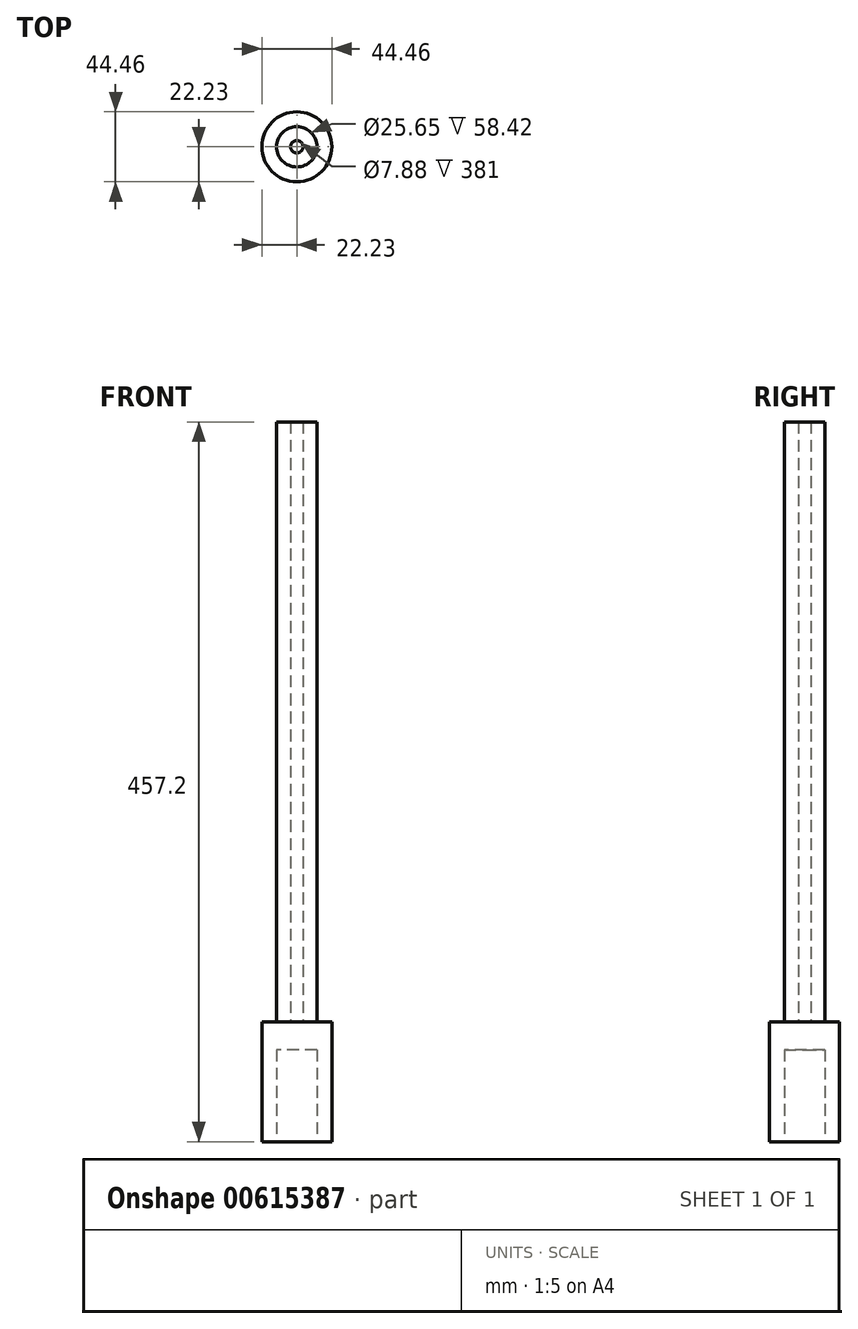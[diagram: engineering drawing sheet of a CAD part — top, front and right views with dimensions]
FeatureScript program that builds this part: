
annotation { "Feature Type Name" : "Feature", "Feature Type Description" : "" }
export const myFeature = defineFeature(function(context is Context, id is Id, definition is map)
    precondition{}
    {
        {
            var Q0;
            Q0=qCreatedBy(makeId("Top.planeOp"),FACE);
            var sketch = newSketch(context, id + "F0", { "sketchPlane" : qUnion([Q0])});
            skCircle(sketch, "E0", {"center": v(0, 0) * mm, "radius": 22.23 * mm});
            skCircle(sketch, "E1", {"center": v(0, 0) * mm, "radius": 12.83 * mm});
            skCircle(sketch, "E2", {"center": v(0, 0) * mm, "radius": 3.94 * mm});
            skSolve(sketch);
        }
        {
            var Q0;
            Q0=qSketchRegion(id+"F0",true);
            var Q1;
            Q1=makeQuery(id+"F0.imprint","IMPRINT",FACE,{"disambiguationData":[TD([[makeQuery(id+"F0.imprint","IMPRINT",EDGE,{"derivedFrom":sQuery(id+"F0.wireOp",EDGE,"E1")}),1.0]])]});
            var Q2;
            Q2=makeQuery(id+"F0.imprint","IMPRINT",FACE,{"disambiguationData":[TD([[makeQuery(id+"F0.imprint","IMPRINT",EDGE,{"derivedFrom":sQuery(id+"F0.wireOp",EDGE,"E2")}),1.0]])]});
            extrude(context, id + "F1", {"entities" : qUnion([Q0, Q1, Q2]), "depth" : 76.2 * mm, "offsetDistance" : 25.4 * mm});
        }
        {
            var Q0;
            Q0=makeQuery(id+"F0.imprint","IMPRINT",FACE,{"disambiguationData":[TD([[makeQuery(id+"F0.imprint","IMPRINT",EDGE,{"derivedFrom":sQuery(id+"F0.wireOp",EDGE,"E1")}),1.0]])]});
            var Q1;
            Q1=makeQuery(id+"F0.imprint","IMPRINT",FACE,{"disambiguationData":[TD([[makeQuery(id+"F0.imprint","IMPRINT",EDGE,{"derivedFrom":sQuery(id+"F0.wireOp",EDGE,"E2")}),1.0]])]});
            extrude(context, id + "F2", {"entities" : qUnion([Q0, Q1]), "operationType" : NewBodyOperationType.REMOVE, "depth" : 58.42 * mm, "offsetDistance" : 25.4 * mm});
        }
        {
            var Q0;
            Q0=makeQuery(id+"F0.imprint","IMPRINT",FACE,{"disambiguationData":[TD([[makeQuery(id+"F0.imprint","IMPRINT",EDGE,{"derivedFrom":sQuery(id+"F0.wireOp",EDGE,"E1")}),1.0]])]});
            extrude(context, id + "F3", {"entities" : qUnion([Q0]), "operationType" : NewBodyOperationType.ADD, "depth" : 457.2 * mm, "offsetDistance" : 25.4 * mm, "hasSecondDirection" : true, "secondDirectionOppositeDirection" : false, "secondDirectionDepth" : 71.63 * mm});
        }
    });
